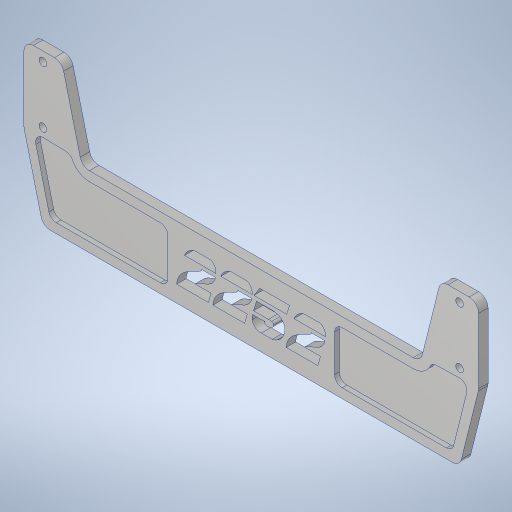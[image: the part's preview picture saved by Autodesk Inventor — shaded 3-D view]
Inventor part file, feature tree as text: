
AUTODESK INVENTOR PART (.ipt)
format: ipt  version: 2023.4 (Build 274418000, 418)  size: 428,544 bytes
history: native  units: in
note: dims shown in document units (in); Inventor stores cm internally (conversion verified against a paired STEP export)
features: sketch x2, extrude x2, fillet x2, hole x1, emboss x1, mirror x1, projected_geometry x1
ambient origin geometry x8: Origin, YZ Plane, XZ Plane, XY Plane, X Axis, Y Axis, Z Axis, Center Point
bodies: Solid1 (feature_tree)
feature tree (10):
  sketch  "Sketch1"  dims[d0=12.0in d1=2.0in]
  extrude  "Extrusion1"  Depth=2.0in
  hole  "Hole1"  [1 undecoded]
  fillet  "Fillet1"  Radius=1.5in
  sketch  "Sketch2"  dims[d2=1.0in d3=1.0in d4=1.5in d5=0.5in d6=0.5in d8=11.0in d9=0.25in d10=0.0in d11=0.201in d12=0.75in d13=0.385in d14=0.25in d15=0.5635in d16=1.0in d17=0.8108in d18=1.875in d19=0.125in d20=0.25in d21=4.0in d22=1.0in d23=3.9in d26=0.25in d27=0.25in d32=0.125in d33=0.0in d34=0.25in d35=0.0in d36=0.2in]
  extrude  "Extrusion2"  Depth=0.5in
  emboss  "Emboss1"
  fillet  "Fillet2"  Radius=0.5in
  mirror  "Mirror1"
  projected_geometry  "Project Cut Edges1"
note: 1 required parameter value undecoded (feature->parameter linkage not recoverable at this tier; creation-order binding heuristic only, values carry confidence <= 0.55)
